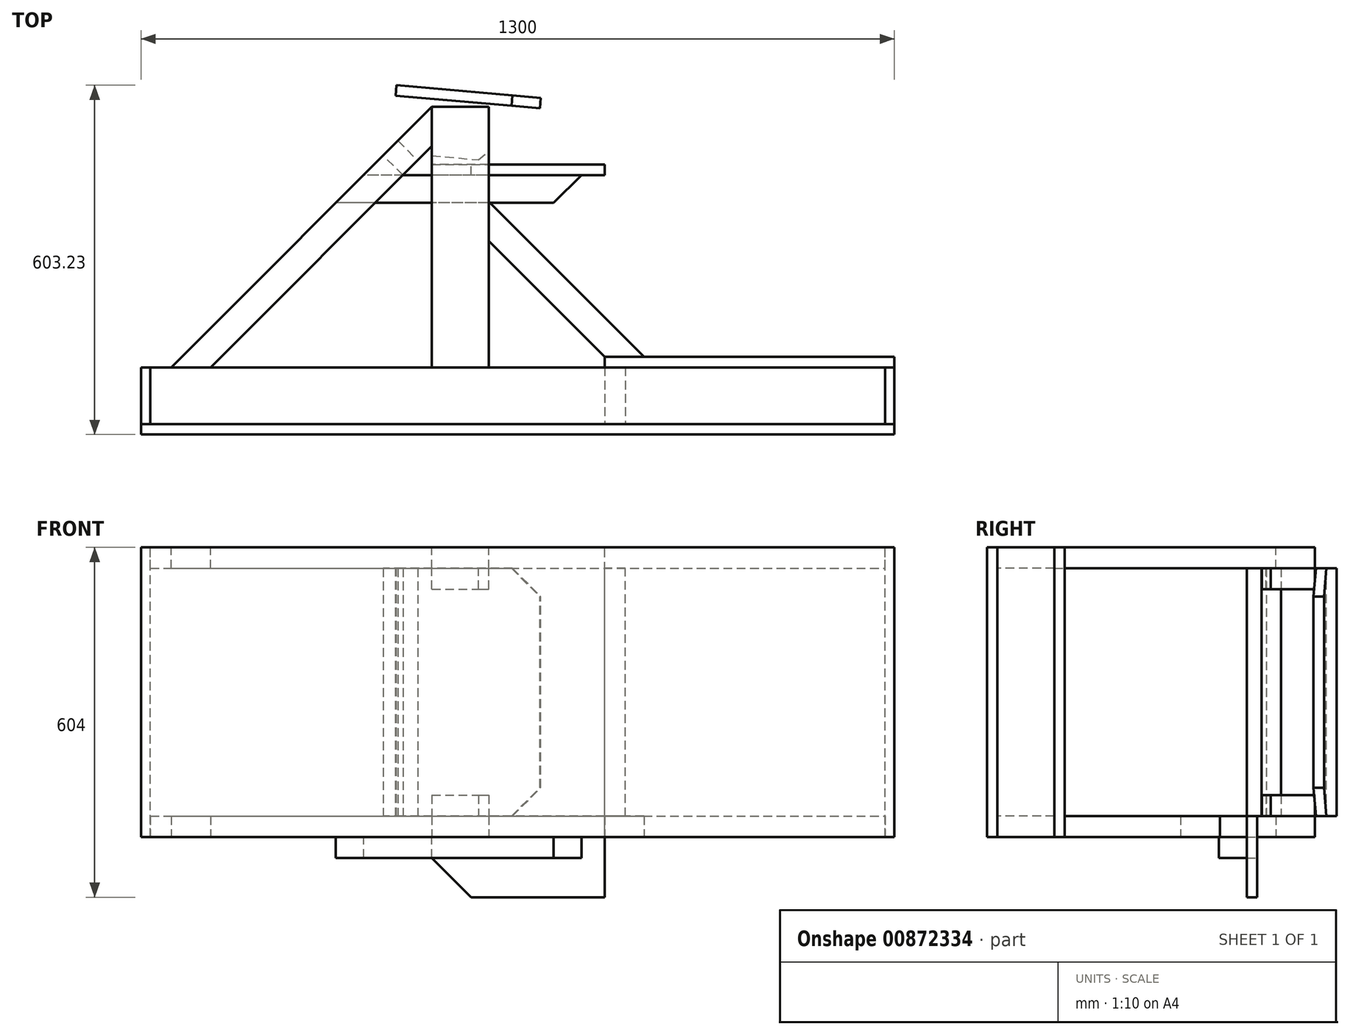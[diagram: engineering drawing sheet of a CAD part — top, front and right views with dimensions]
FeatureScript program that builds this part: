
annotation { "Feature Type Name" : "Feature", "Feature Type Description" : "" }
export const myFeature = defineFeature(function(context is Context, id is Id, definition is map)
    precondition{}
    {
        {
            var Q0;
            Q0=qCreatedBy(makeId("Top.planeOp"),FACE);
            var sketch = newSketch(context, id + "F0", { "sketchPlane" : qUnion([Q0])});
            skLineSegment(sketch, "E0.bottom", {"start": v(0, 0) * mm, "end": v(1268, 0) * mm});
            skLineSegment(sketch, "E0.top", {"start": v(0, -98) * mm, "end": v(1268, -98) * mm});
            skLineSegment(sketch, "E0.left", {"start": v(0, 0) * mm, "end": v(0, -98) * mm});
            skLineSegment(sketch, "E0.right", {"start": v(1268, 0) * mm, "end": v(1268, -98) * mm});
            skLineSegment(sketch, "E1.bottom", {"start": v(486, 0) * mm, "end": v(584, 0) * mm});
            skLineSegment(sketch, "E1.top", {"start": v(486, 450) * mm, "end": v(584, 450) * mm});
            skLineSegment(sketch, "E1.left", {"start": v(486, 0) * mm, "end": v(486, 450) * mm});
            skLineSegment(sketch, "E1.right", {"start": v(584, 0) * mm, "end": v(584, 450) * mm});
            skLineSegment(sketch, "E2", {"start": v(36, 0) * mm, "end": v(486, 450) * mm});
            skLineSegment(sketch, "E3", {"start": v(103.88, 0) * mm, "end": v(486, 382.12) * mm});
            skLineSegment(sketch, "E4.bottom", {"start": v(1268, -98) * mm, "end": v(1284, -98) * mm});
            skLineSegment(sketch, "E4.top", {"start": v(1268, 0) * mm, "end": v(1284, 0) * mm});
            skLineSegment(sketch, "E4.left", {"start": v(1268, -98) * mm, "end": v(1268, 0) * mm});
            skLineSegment(sketch, "E4.right", {"start": v(1284, -98) * mm, "end": v(1284, 0) * mm});
            skLineSegment(sketch, "E5.bottom", {"start": v(0, -98) * mm, "end": v(-16, -98) * mm});
            skLineSegment(sketch, "E5.top", {"start": v(0, 0) * mm, "end": v(-16, 0) * mm});
            skLineSegment(sketch, "E5.left", {"start": v(0, -98) * mm, "end": v(0, 0) * mm});
            skLineSegment(sketch, "E5.right", {"start": v(-16, -98) * mm, "end": v(-16, 0) * mm});
            skLineSegment(sketch, "E6.bottom", {"start": v(1284, 0) * mm, "end": v(784, 0) * mm});
            skLineSegment(sketch, "E6.top", {"start": v(1284, 18) * mm, "end": v(784, 18) * mm});
            skLineSegment(sketch, "E6.left", {"start": v(1284, 0) * mm, "end": v(1284, 18) * mm});
            skLineSegment(sketch, "E6.right", {"start": v(784, 0) * mm, "end": v(784, 18) * mm});
            skLineSegment(sketch, "E7", {"start": v(1284, -98) * mm, "end": v(1284, -116) * mm});
            skLineSegment(sketch, "E8", {"start": v(1284, -116) * mm, "end": v(-16, -116) * mm});
            skLineSegment(sketch, "E9", {"start": v(-16, -116) * mm, "end": v(-16, -98) * mm});
            skSolve(sketch);
        }
        {
            var Q0;
            Q0=makeQuery(id+"F0.imprint","IMPRINT",FACE,{"disambiguationData":[TD([[makeQuery(id+"F0.imprint","IMPRINT",EDGE,{"derivedFrom":sQuery(id+"F0.wireOp",EDGE,"E0.top")}),-1.0]])]});
            extrude(context, id + "F1", {"entities" : qUnion([Q0]), "oppositeDirection" : true, "depth" : 500 * mm, "offsetDistance" : 25 * mm});
        }
        {
            var Q0;
            Q0=makeQuery(id+"F0.imprint","IMPRINT",FACE,{"disambiguationData":[TD([[makeQuery(id+"F0.imprint","IMPRINT",EDGE,{"derivedFrom":sQuery(id+"F0.wireOp",EDGE,"E0.top")}),1.0]])]});
            extrude(context, id + "F2", {"entities" : qUnion([Q0]), "oppositeDirection" : true, "depth" : 36 * mm, "offsetDistance" : 25 * mm});
        }
        {
            var Q0;
            {var subQ1=sQuery(id+"F0.wireOp",EDGE,"E1.top");Q0=makeQuery(id+"F0.imprint","IMPRINT",FACE,{"disambiguationData":[TD([[makeQuery(id+"F0.imprint","IMPRINT",EDGE,{"derivedFrom":subQ1}),-1.0]])]});}
            extrude(context, id + "F3", {"entities" : qUnion([Q0]), "oppositeDirection" : true, "depth" : 36 * mm, "offsetDistance" : 25 * mm});
        }
        {
            var Q0;
            {var subQ0=sQuery(id+"F0.wireOp",EDGE,"E2");Q0=makeQuery(id+"F0.imprint","IMPRINT",FACE,{"disambiguationData":[TD([[makeQuery(id+"F0.imprint","IMPRINT",EDGE,{"derivedFrom":subQ0}),-1.0]])]});}
            extrude(context, id + "F4", {"entities" : qUnion([Q0]), "oppositeDirection" : true, "depth" : 36 * mm, "offsetDistance" : 25 * mm});
        }
        {
            var Q0;
            {var subQ2=sQuery(id+"F0.wireOp",EDGE,"E4.top");Q0=makeQuery(id+"F0.imprint","IMPRINT",FACE,{"disambiguationData":[TD([[makeQuery(id+"F0.imprint","IMPRINT",EDGE,{"derivedFrom":subQ2}),1.0]])]});}
            extrude(context, id + "F5", {"entities" : qUnion([Q0]), "oppositeDirection" : true, "depth" : 500 * mm, "offsetDistance" : 25 * mm});
        }
        {
            var Q0;
            Q0=makeQuery(id+"F0.imprint","IMPRINT",FACE,{"disambiguationData":[TD([[makeQuery(id+"F0.imprint","IMPRINT",EDGE,{"derivedFrom":sQuery(id+"F0.wireOp",EDGE,"E0.right")}),1.0]])]});
            extrude(context, id + "F6", {"entities" : qUnion([Q0]), "oppositeDirection" : true, "depth" : 500 * mm, "offsetDistance" : 25 * mm});
        }
        {
            var Q0;
            Q0=makeQuery(id+"F3.opExtrude","CAP_FACE",FACE,{"disambiguationData":[OSD([sQuery(id+"F0.wireOp",EDGE,"E0.bottom"),sQuery(id+"F0.wireOp",EDGE,"E1.top"),sQuery(id+"F0.wireOp",EDGE,"E1.left"),sQuery(id+"F0.wireOp",EDGE,"E1.right")])],"isStart":false});
            var sketch = newSketch(context, id + "F7", { "sketchPlane" : qUnion([Q0])});
            skLineSegment(sketch, "E10", {"start": v(424.79, -487.23) * mm, "end": v(414.68, -371.67) * mm});
            skLineSegment(sketch, "E11", {"start": v(414.68, -371.67) * mm, "end": v(663.72, -349.88) * mm});
            skLineSegment(sketch, "E12", {"start": v(663.72, -349.88) * mm, "end": v(673.83, -465.44) * mm});
            skLineSegment(sketch, "E13", {"start": v(673.83, -465.44) * mm, "end": v(424.79, -487.23) * mm});
            skLineSegment(sketch, "E14", {"start": v(423.22, -469.3) * mm, "end": v(672.27, -447.5) * mm});
            skLineSegment(sketch, "E15", {"start": v(566.1, -358.42) * mm, "end": v(672.27, -447.5) * mm});
            skLineSegment(sketch, "E16", {"start": v(418.88, -419.67) * mm, "end": v(462.68, -367.47) * mm});
            skLineSegment(sketch, "E17", {"start": v(619.18, -402.96) * mm, "end": v(623.45, -451.78) * mm});
            skSolve(sketch);
        }
        {
            var Q0;
            {var subQ3=sQuery(id+"F7.wireOp",EDGE,"E17");Q0=makeQuery(id+"F7.imprint","IMPRINT",FACE,{"disambiguationData":[TD([[makeQuery(id+"F7.imprint","IMPRINT",EDGE,{"derivedFrom":subQ3}),-1.0]])]});}
            var Q1;
            {var subQ1=makeQuery(id+"F3.opExtrude","CAP_EDGE",EDGE,{"disambiguationData":[OSD([sQuery(id+"F0.wireOp",EDGE,"E1.top")])],"isStart":false});Q1=makeQuery(id+"F7.imprint","IMPRINT",FACE,{"disambiguationData":[TD([[makeQuery(id+"F7.imprint","IMPRINT",EDGE,{"derivedFrom":subQ1}),1.0]])]});}
            extrude(context, id + "F8", {"entities" : qUnion([Q0, Q1]), "depth" : 36 * mm, "offsetDistance" : 25 * mm});
        }
        {
            var Q0;
            {var subQ0=sQuery(id+"F7.wireOp",EDGE,"E13");Q0=makeQuery(id+"F7.imprint","IMPRINT",FACE,{"disambiguationData":[TD([[makeQuery(id+"F7.imprint","IMPRINT",EDGE,{"derivedFrom":subQ0}),-1.0]])]});}
            extrude(context, id + "F9", {"entities" : qUnion([Q0]), "depth" : (500 - 2 * 36) * mm, "offsetDistance" : 25 * mm});
        }
        {
            var Q0;
            Q0=makeQuery(id+"F0.imprint","IMPRINT",FACE,{"disambiguationData":[TD([[makeQuery(id+"F0.imprint","IMPRINT",EDGE,{"derivedFrom":sQuery(id+"F0.wireOp",EDGE,"E0.top")}),-1.0]])]});
            var Q1;
            Q1=makeQuery(id+"F1.opExtrude","CAP_FACE",FACE,{"disambiguationData":[OSD([sQuery(id+"F0.wireOp",EDGE,"E0.top"),sQuery(id+"F0.wireOp",EDGE,"E4.bottom"),sQuery(id+"F0.wireOp",EDGE,"E5.bottom"),sQuery(id+"F0.wireOp",EDGE,"E7"),sQuery(id+"F0.wireOp",EDGE,"E8"),sQuery(id+"F0.wireOp",EDGE,"E9")])],"isStart":false});
            cPlane(context, id + "F10", {"entities" : qUnion([Q0, Q1]), "cplaneType" : CPlaneType.MID_PLANE, "offset" : 25 * mm, "width" : 150 * mm, "height" : 150 * mm});
        }
        {
            var Q0;
            Q0=makeQuery(id+"F3.opExtrude","SWEPT_BODY",BODY,{"disambiguationData":[OSD([sQuery(id+"F0.wireOp",EDGE,"E0.bottom"),sQuery(id+"F0.wireOp",EDGE,"E1.top"),sQuery(id+"F0.wireOp",EDGE,"E1.left"),sQuery(id+"F0.wireOp",EDGE,"E1.right")])]});
            var Q1;
            Q1=makeQuery(id+"F2.opExtrude","SWEPT_BODY",BODY,{"disambiguationData":[OSD([sQuery(id+"F0.wireOp",EDGE,"E0.bottom"),sQuery(id+"F0.wireOp",EDGE,"E0.top"),sQuery(id+"F0.wireOp",EDGE,"E0.left"),sQuery(id+"F0.wireOp",EDGE,"E0.right")])]});
            var Q2;
            Q2=makeQuery(id+"F4.opExtrude","SWEPT_BODY",BODY,{"disambiguationData":[OSD([sQuery(id+"F0.wireOp",EDGE,"E0.bottom"),sQuery(id+"F0.wireOp",EDGE,"E1.left"),sQuery(id+"F0.wireOp",EDGE,"E2"),sQuery(id+"F0.wireOp",EDGE,"E3")])]});
            var Q3;
            Q3=makeQuery(id+"F8.opExtrude","SWEPT_BODY",BODY,{"disambiguationData":[OSD([sQuery(id+"F7.wireOp",EDGE,"E10"),sQuery(id+"F7.wireOp",EDGE,"E11"),sQuery(id+"F7.wireOp",EDGE,"E14"),sQuery(id+"F7.wireOp",EDGE,"E15")])]});
            var Q4;
            Q4=qCreatedBy(id+"F10.planeOp",FACE);
            mirror(context, id + "F11", {"entities" : qUnion([Q0, Q1, Q2, Q3]), "mirrorPlane" : qUnion([Q4])});
        }
        {
            var Q0;
            Q0=makeQuery(id+"F1.opExtrude","SWEPT_FACE",FACE,{"disambiguationData":[OSD([sQuery(id+"F0.wireOp",EDGE,"E9")])]});
            var Q1;
            Q1=makeQuery(id+"F1.opExtrude","SWEPT_FACE",FACE,{"disambiguationData":[OSD([sQuery(id+"F0.wireOp",EDGE,"E7")])]});
            cPlane(context, id + "F12", {"entities" : qUnion([Q0, Q1]), "cplaneType" : CPlaneType.MID_PLANE, "offset" : 25 * mm, "width" : 150 * mm, "height" : 150 * mm});
        }
        {
            var Q0;
            Q0=makeQuery(id+"F6.opExtrude","SWEPT_BODY",BODY,{"disambiguationData":[OSD([sQuery(id+"F0.wireOp",EDGE,"E0.right"),sQuery(id+"F0.wireOp",EDGE,"E4.bottom"),sQuery(id+"F0.wireOp",EDGE,"E4.top"),sQuery(id+"F0.wireOp",EDGE,"E4.right")])]});
            var Q1;
            Q1=qCreatedBy(id+"F12.planeOp",FACE);
            mirror(context, id + "F13", {"entities" : qUnion([Q0]), "mirrorPlane" : qUnion([Q1])});
        }
        {
            var Q0;
            Q0=makeQuery(id+"F5.opExtrude","SWEPT_FACE",FACE,{"disambiguationData":[OSD([sQuery(id+"F0.wireOp",EDGE,"E6.right")])]});
            var sketch = newSketch(context, id + "F14", { "sketchPlane" : qUnion([Q0])});
            skLineSegment(sketch, "E18", {"start": v(0, -464) * mm, "end": v(98, -464) * mm});
            skLineSegment(sketch, "E19", {"start": v(98, -464) * mm, "end": v(98, -36) * mm});
            skLineSegment(sketch, "E20", {"start": v(98, -36) * mm, "end": v(0, -36) * mm});
            skLineSegment(sketch, "E21", {"start": v(0, -36) * mm, "end": v(0, -464) * mm});
            skSolve(sketch);
        }
        {
            var Q0;
            Q0=makeQuery(id+"F14.imprint","IMPRINT",FACE,{"disambiguationData":[TD([[makeQuery(id+"F14.imprint","IMPRINT",EDGE,{"derivedFrom":sQuery(id+"F14.wireOp",EDGE,"E18")}),1.0]])]});
            extrude(context, id + "F15", {"entities" : qUnion([Q0]), "oppositeDirection" : true, "depth" : 36 * mm, "offsetDistance" : 25 * mm});
        }
        {
            var Q0;
            Q0=makeQuery(id+"F11.opPattern","COPY",FACE,{"derivedFrom":makeQuery(id+"F3.opExtrude","CAP_FACE",FACE,{"disambiguationData":[OSD([sQuery(id+"F0.wireOp",EDGE,"E0.bottom"),sQuery(id+"F0.wireOp",EDGE,"E1.top"),sQuery(id+"F0.wireOp",EDGE,"E1.left"),sQuery(id+"F0.wireOp",EDGE,"E1.right")])],"isStart":true}),"instanceName":"1"});
            var sketch = newSketch(context, id + "F16", { "sketchPlane" : qUnion([Q0])});
            skLineSegment(sketch, "E22", {"start": v(486, -350) * mm, "end": v(784, -350) * mm});
            skLineSegment(sketch, "E23", {"start": v(784, -350) * mm, "end": v(784, -332) * mm});
            skLineSegment(sketch, "E24", {"start": v(784, -332) * mm, "end": v(486, -332) * mm});
            skLineSegment(sketch, "E25", {"start": v(486, -332) * mm, "end": v(486, -350) * mm});
            skLineSegment(sketch, "E26", {"start": v(744, -332) * mm, "end": v(696, -284) * mm});
            skLineSegment(sketch, "E27", {"start": v(696, -284) * mm, "end": v(320, -284) * mm});
            skLineSegment(sketch, "E28", {"start": v(320, -284) * mm, "end": v(368, -332) * mm});
            skLineSegment(sketch, "E29", {"start": v(368, -332) * mm, "end": v(744, -332) * mm});
            skSolve(sketch);
        }
        {
            var Q0;
            {var subQ0=sQuery(id+"F16.wireOp",EDGE,"E27");var subQ1=makeQuery(id+"F11.opPattern","COPY",EDGE,{"derivedFrom":makeQuery(id+"F3.opExtrude","CAP_EDGE",EDGE,{"disambiguationData":[OSD([sQuery(id+"F0.wireOp",EDGE,"E1.right")])],"isStart":true}),"instanceName":"1"});var subQ2=makeQuery(id+"F16.imprint","INTERSECT",VERTEX,{"derivedFrom":[subQ1,subQ0]});Q0=makeQuery(id+"F16.imprint","IMPRINT",FACE,{"disambiguationData":[TD([[makeQuery(id+"F16.imprint","IMPRINT",EDGE,{"disambiguationData":[TD([[subQ2,-1.0]])],"derivedFrom":subQ0}),1.0]])]});}
            var Q1;
            {var subQ0=sQuery(id+"F16.wireOp",EDGE,"E26");Q1=makeQuery(id+"F16.imprint","IMPRINT",FACE,{"disambiguationData":[TD([[makeQuery(id+"F16.imprint","IMPRINT",EDGE,{"derivedFrom":subQ0}),1.0]])]});}
            var Q2;
            {var subQ0=sQuery(id+"F16.wireOp",EDGE,"E28");Q2=makeQuery(id+"F16.imprint","IMPRINT",FACE,{"disambiguationData":[TD([[makeQuery(id+"F16.imprint","IMPRINT",EDGE,{"derivedFrom":subQ0}),1.0]])]});}
            extrude(context, id + "F17", {"entities" : qUnion([Q0, Q1, Q2]), "depth" : 36 * mm, "offsetDistance" : 25 * mm});
        }
        {
            var Q0;
            {var subQ1=sQuery(id+"F16.wireOp",EDGE,"E23");Q0=makeQuery(id+"F16.imprint","IMPRINT",FACE,{"disambiguationData":[TD([[makeQuery(id+"F16.imprint","IMPRINT",EDGE,{"derivedFrom":subQ1}),1.0]])]});}
            var Q1;
            {var subQ0=sQuery(id+"F16.wireOp",EDGE,"E25");Q1=makeQuery(id+"F16.imprint","IMPRINT",FACE,{"disambiguationData":[TD([[makeQuery(id+"F16.imprint","IMPRINT",EDGE,{"derivedFrom":subQ0}),1.0]])]});}
            extrude(context, id + "F18", {"entities" : qUnion([Q0, Q1]), "depth" : (140 - 36) * mm, "offsetDistance" : 25 * mm, "hasSecondDirection" : true, "secondDirectionOppositeDirection" : true, "secondDirectionDepth" : 36 * mm});
        }
        {
            var Q0;
            Q0=makeQuery(id+"F18.opExtrude","SWEPT_FACE",FACE,{"disambiguationData":[OSD([sQuery(id+"F16.wireOp",EDGE,"E22")])]});
            var sketch = newSketch(context, id + "F19", { "sketchPlane" : qUnion([Q0])});
            skLineSegment(sketch, "E30", {"start": v(-584, -464) * mm, "end": v(-584, -500) * mm});
            skLineSegment(sketch, "E31", {"start": v(-584, -500) * mm, "end": v(-486, -500) * mm});
            skLineSegment(sketch, "E32", {"start": v(-486, -500) * mm, "end": v(-486, -464) * mm});
            skLineSegment(sketch, "E33", {"start": v(-486, -464) * mm, "end": v(-584, -464) * mm});
            skLineSegment(sketch, "E34", {"start": v(-486, -536) * mm, "end": v(-554, -604) * mm});
            skLineSegment(sketch, "E35", {"start": v(-554, -604) * mm, "end": v(-486, -604) * mm});
            skLineSegment(sketch, "E36", {"start": v(-486, -604) * mm, "end": v(-486, -536) * mm});
            skSolve(sketch);
        }
        {
            var Q0;
            Q0 = qSketchRegion(id + "F19", true);
            extrude(context, id + "F20", {"entities" : qUnion([Q0]), "operationType" : NewBodyOperationType.REMOVE, "endBound" : BoundingType.UP_TO_NEXT, "oppositeDirection" : true, "depth" : 25 * mm, "offsetDistance" : 25 * mm});
        }
        {
            var Q0;
            Q0=makeQuery(id+"F11.opPattern","COPY",FACE,{"derivedFrom":makeQuery(id+"F3.opExtrude","CAP_FACE",FACE,{"disambiguationData":[OSD([sQuery(id+"F0.wireOp",EDGE,"E0.bottom"),sQuery(id+"F0.wireOp",EDGE,"E1.top"),sQuery(id+"F0.wireOp",EDGE,"E1.left"),sQuery(id+"F0.wireOp",EDGE,"E1.right")])],"isStart":true}),"instanceName":"1"});
            var sketch = newSketch(context, id + "F21", { "sketchPlane" : qUnion([Q0])});
            skLineSegment(sketch, "E37", {"start": v(784, -18) * mm, "end": v(584, -218) * mm});
            skLineSegment(sketch, "E38", {"start": v(584, -218) * mm, "end": v(584, -285.88) * mm});
            skLineSegment(sketch, "E39", {"start": v(584, -285.88) * mm, "end": v(851.88, -18) * mm});
            skLineSegment(sketch, "E40", {"start": v(851.88, -18) * mm, "end": v(784, -18) * mm});
            skSolve(sketch);
        }
        {
            var Q0;
            Q0=makeQuery(id+"F21.imprint","IMPRINT",FACE,{"disambiguationData":[TD([[makeQuery(id+"F21.imprint","IMPRINT",EDGE,{"derivedFrom":sQuery(id+"F21.wireOp",EDGE,"E37")}),1.0]])]});
            extrude(context, id + "F22", {"entities" : qUnion([Q0]), "oppositeDirection" : true, "depth" : 36 * mm, "offsetDistance" : 25 * mm});
        }
        {
            var Q0;
            Q0=makeQuery(id+"F11.opPattern","COPY",FACE,{"derivedFrom":makeQuery(id+"F4.opExtrude","CAP_FACE",FACE,{"disambiguationData":[OSD([sQuery(id+"F0.wireOp",EDGE,"E0.bottom"),sQuery(id+"F0.wireOp",EDGE,"E1.left"),sQuery(id+"F0.wireOp",EDGE,"E2"),sQuery(id+"F0.wireOp",EDGE,"E3")])],"isStart":false}),"instanceName":"1"});
            var sketch = newSketch(context, id + "F23", { "sketchPlane" : qUnion([Q0])});
            skLineSegment(sketch, "E41", {"start": v(427.4, 391.4) * mm, "end": v(461.34, 357.46) * mm});
            skLineSegment(sketch, "E42", {"start": v(461.34, 357.46) * mm, "end": v(435.88, 332) * mm});
            skLineSegment(sketch, "E43", {"start": v(435.88, 332) * mm, "end": v(401.94, 365.94) * mm});
            skLineSegment(sketch, "E44", {"start": v(401.94, 365.94) * mm, "end": v(427.4, 391.4) * mm});
            skSolve(sketch);
        }
        {
            var Q0;
            Q0=makeQuery(id+"F23.imprint","IMPRINT",FACE,{"disambiguationData":[TD([[makeQuery(id+"F23.imprint","IMPRINT",EDGE,{"derivedFrom":sQuery(id+"F23.wireOp",EDGE,"E41")}),-1.0]])]});
            extrude(context, id + "F24", {"entities" : qUnion([Q0]), "endBound" : BoundingType.UP_TO_NEXT, "depth" : 25 * mm, "offsetDistance" : 25 * mm});
        }
        {
            var Q0;
            Q0=makeQuery(id+"F9.opExtrude","SWEPT_FACE",FACE,{"disambiguationData":[OSD([sQuery(id+"F7.wireOp",EDGE,"E14")])]});
            var sketch = newSketch(context, id + "F25", { "sketchPlane" : qUnion([Q0])});
            skLineSegment(sketch, "E45", {"start": v(581.7, -36) * mm, "end": v(630.7, -85) * mm});
            skLineSegment(sketch, "E46", {"start": v(630.7, -85) * mm, "end": v(630.7, -36) * mm});
            skLineSegment(sketch, "E47", {"start": v(630.7, -36) * mm, "end": v(581.7, -36) * mm});
            skLineSegment(sketch, "E48", {"start": v(380.7, -250) * mm, "end": v(630.7, -250) * mm, "construction": true});
            skLineSegment(sketch, "E49.MirrorCS", {"start": v(630.7, -415) * mm, "end": v(630.7, -464) * mm});
            skLineSegment(sketch, "E50.MirrorCS", {"start": v(581.7, -464) * mm, "end": v(630.7, -415) * mm});
            skLineSegment(sketch, "E51.MirrorCS", {"start": v(630.7, -464) * mm, "end": v(581.7, -464) * mm});
            skSolve(sketch);
        }
        {
            var Q0;
            Q0 = qSketchRegion(id + "F25", true);
            extrude(context, id + "F26", {"entities" : qUnion([Q0]), "operationType" : NewBodyOperationType.REMOVE, "endBound" : BoundingType.UP_TO_NEXT, "oppositeDirection" : true, "depth" : 25 * mm, "offsetDistance" : 25 * mm});
        }
    });
